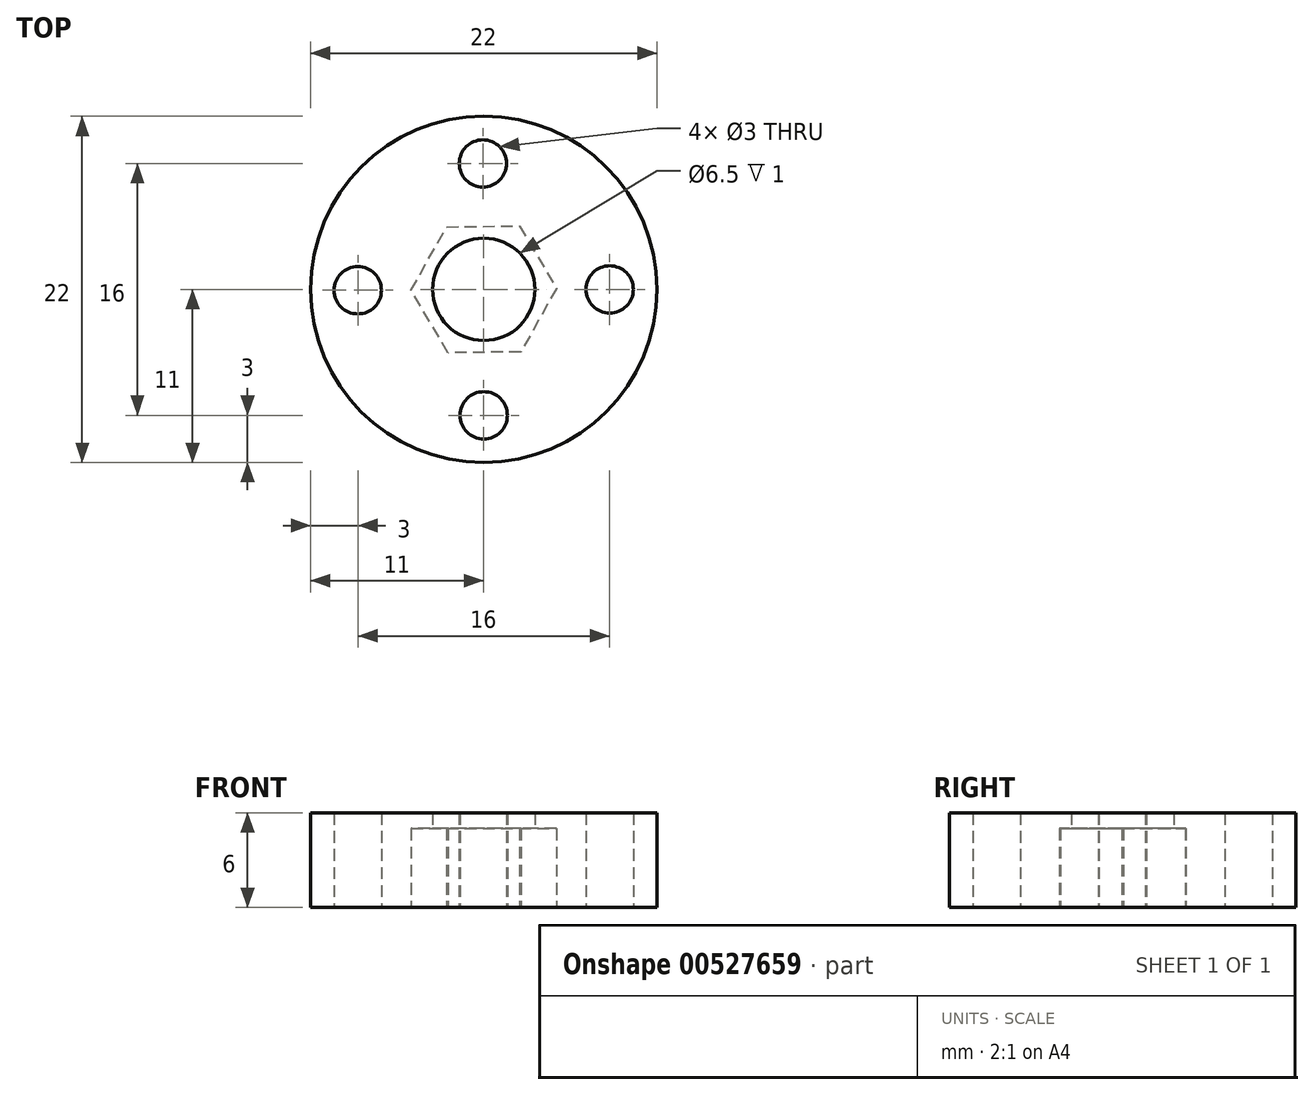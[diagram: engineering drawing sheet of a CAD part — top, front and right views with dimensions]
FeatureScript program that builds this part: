
annotation { "Feature Type Name" : "Feature", "Feature Type Description" : "" }
export const myFeature = defineFeature(function(context is Context, id is Id, definition is map)
    precondition{}
    {
        {
            var Q0;
            Q0=qCreatedBy(makeId("Top.planeOp"),FACE);
            var sketch = newSketch(context, id + "F0", { "sketchPlane" : qUnion([Q0])});
            skCircle(sketch, "E0.cCircle", {"center": v(0, 0) * mm, "radius": 4 * mm, "construction": true});
            skLineSegment(sketch, "E0.0", {"start": v(2.26, 4.03) * mm, "end": v(4.62, 0.06) * mm});
            skLineSegment(sketch, "E0.1", {"start": v(4.62, 0.06) * mm, "end": v(2.36, -3.97) * mm});
            skLineSegment(sketch, "E0.2", {"start": v(2.36, -3.97) * mm, "end": v(-2.26, -4.03) * mm});
            skLineSegment(sketch, "E0.3", {"start": v(-2.26, -4.03) * mm, "end": v(-4.62, -0.06) * mm});
            skLineSegment(sketch, "E0.4", {"start": v(-4.62, -0.06) * mm, "end": v(-2.36, 3.97) * mm});
            skLineSegment(sketch, "E0.5", {"start": v(-2.36, 3.97) * mm, "end": v(2.26, 4.03) * mm});
            skPoint(sketch, "E0.0.midPoint", {"position": v(3.44, 2.04) * mm});
            skCircle(sketch, "E1", {"center": v(0, 0) * mm, "radius": 11 * mm});
            skCircle(sketch, "E2", {"center": v(0, 0) * mm, "radius": 8 * mm, "construction": true});
            skLineSegment(sketch, "E3", {"start": v(0, 0) * mm, "end": v(8, 0) * mm});
            skLineSegment(sketch, "E4", {"start": v(0, 0) * mm, "end": v(-8, -0.06) * mm});
            skLineSegment(sketch, "E5", {"start": v(0, 0) * mm, "end": v(-0.06, 8) * mm});
            skLineSegment(sketch, "E6", {"start": v(0, 0) * mm, "end": v(0, -8) * mm});
            skCircle(sketch, "E7", {"center": v(-0.06, 8) * mm, "radius": 1.5 * mm});
            skCircle(sketch, "E8", {"center": v(8, 0) * mm, "radius": 1.5 * mm});
            skCircle(sketch, "E9", {"center": v(0, -8) * mm, "radius": 1.5 * mm});
            skCircle(sketch, "E10", {"center": v(-8, -0.06) * mm, "radius": 1.5 * mm});
            skSolve(sketch);
        }
        {
            var Q0;
            {var subQ1=sQuery(id+"F0.wireOp",EDGE,"E0.0");Q0=makeQuery(id+"F0.imprint","IMPRINT",FACE,{"disambiguationData":[TD([[makeQuery(id+"F0.imprint","IMPRINT",EDGE,{"derivedFrom":subQ1}),1.0]])]});}
            extrude(context, id + "F1", {"entities" : qUnion([Q0]), "depth" : 5 * mm, "offsetDistance" : 25 * mm});
        }
        {
            var Q0;
            Q0=makeQuery(id+"F1.opExtrude","CAP_FACE",FACE,{"disambiguationData":[OSD([sQuery(id+"F0.wireOp",EDGE,"E0.0"),sQuery(id+"F0.wireOp",EDGE,"E0.1"),sQuery(id+"F0.wireOp",EDGE,"E0.2"),sQuery(id+"F0.wireOp",EDGE,"E0.3"),sQuery(id+"F0.wireOp",EDGE,"E0.4"),sQuery(id+"F0.wireOp",EDGE,"E0.5"),sQuery(id+"F0.wireOp",EDGE,"E1"),sQuery(id+"F0.wireOp",EDGE,"E7"),sQuery(id+"F0.wireOp",EDGE,"E8"),sQuery(id+"F0.wireOp",EDGE,"E9"),sQuery(id+"F0.wireOp",EDGE,"E10")])],"isStart":false});
            var sketch = newSketch(context, id + "F2", { "sketchPlane" : qUnion([Q0])});
            skCircle(sketch, "E11", {"center": v(0, 0) * mm, "radius": 11 * mm});
            skPoint(sketch, "E11.first.point", {"position": v(0, -11) * mm});
            skPoint(sketch, "E11.second.point", {"position": v(0.05, 11) * mm});
            skPoint(sketch, "E11.second.point.positionSnap0", {"position": v(0.05, -4) * mm});
            skPoint(sketch, "E11.third.point", {"position": v(-7.4, 8.14) * mm});
            skCircle(sketch, "E12", {"center": v(0, 0) * mm, "radius": 3.25 * mm});
            skSolve(sketch);
        }
        {
            var Q0;
            Q0=makeQuery(id+"F2.imprint","IMPRINT",FACE,{"disambiguationData":[TD([[makeQuery(id+"F2.imprint","IMPRINT",EDGE,{"derivedFrom":sQuery(id+"F2.wireOp",EDGE,"E12")}),-1.0]])]});
            var Q1;
            Q1=makeQuery(id+"F2.imprint","IMPRINT",FACE,{"disambiguationData":[TD([[makeQuery(id+"F2.imprint","IMPRINT",EDGE,{"derivedFrom":sQuery(id+"F2.wireOp",EDGE,"E11")}),1.0]])]});
            extrude(context, id + "F3", {"entities" : qUnion([Q0, Q1]), "operationType" : NewBodyOperationType.ADD, "depth" : 1 * mm, "offsetDistance" : 25 * mm});
        }
    });
